# Revit family: HVAC_Mechanical-Ventilation_Ice-Air_HWCAC_Horizontal
name_source: partatom
category: Mechanical Equipment
revit_build: Autodesk Revit 2015 (Build: 20140606_1530(x64)
units: mm (PartAtom-declared; Revit-internal decimal feet)

## types (11) — shared parameters
2-pipe Inlet Description = Water Inlet Connection
2-pipe Outlet Description = Water Outlet Connection
Air Filter Material = Plastic - Ice_Air - Blue
BIMobject category = Air Conditioning
BIMobject category code = hvac-air-con
BIMobject main category = HVAC
BIMobject main category code = hvac
Brand url = http://www.ice-air.com
Condensate Connection = 0.75 "
Condensate Drain Description = Condensate Drain Connection
Date of publishing = 1/30/2014
Default Elevation = 48 "
Description = Conserve floor space with ICE AIRs Horizontal WSHPs - flexible control options, variable air discharge outlets, and easy service access provide superior design and installation options.
Design country = United States
Discharge Position = 12 "
Duct Description = Supply Air
Edition number = 1
Frequency = 60 Hz
IFC Classification = Heat Exchanger
Manufacturer = Ice Air
Manufacturer country = United States
Manufacturer name = Ice Air
Masterformat 2014 Code = 23 00 00
Masterformat 2014 Description = Heating, Ventilating, and Air Conditioning (HVAC)
NBS Reference Code = 03-03
NBS Reference Description = Air Conditioning Units
OmniClass Code = 23-33 39 11
OmniClass Description = Air Conditioners
Phase = 1
Product Guid = 5dc7aca0-5e98-4522-918c-9e6a5670b57e
Product SKU = horizontal_wshp_hybrid
Product data url = https://bimobject.com
Product family = Hybrid WCAC
Product group = Horizontal
Product url = http://www.ice-air.com
QR code = http://bimobject.com
Return Lenght = 25.4 "
Return Offset = 1.54 "
Steel Material = Steel - Ice_Air - Galvanized
Technical description = http://www.ice-air.com
UNSPSC Code = 40101701
URL = http://www.ice-air.com
Uniclass 1.4 Code = JU
Uniclass 1.4 Description = Ventilation and air conditioning systems
Uniclass 2.0 Code = PR-03-03
Uniclass 2.0 Description = Air Conditioning Units
Uniclass 2015 Code = EF_65_80
Uniclass 2015 Name = Air conditioning
Uniformat II Code = D3090
Uniformat II Description = Other HVAC Systems & Equipment
Voltage = 230 V
Voltage (Range) = 208 - 230 V
Weight Net (Kg) = 0
zero-valued in all types: Nominal height, Nominal width

## per-type parameters (varying)
| type | Air Flow | Discharge Height | Discharge Width | Energy Efficiency Rating w/ECM | Energy Efficiency Rating w/PSC | Flow Rate | Height | Inlet/Outlet Connection | Length | Total Cooling Capacity | Total Heating Capacity @ 105F EWT | Total Heating Capacity @ 120F EWT | Total Heating Capacity @ 95F EWT | Weight | Width | z Type |
| 8HHW09 | 300.0 CFM | 5 " | 10 " | 14.5 | 14 | 2.3 GPM | 12 " | 0.5 " | 34 " | 9300 Btu/h | 8500 Btu/h | 10500 Btu/h | 6300 Btu/h | 130 lbm | 20 " | 1 |
| 8HHW12 | 400.0 CFM | 5 " | 10 " | 14.1 | 13.5 | 3.0 GPM | 12 " | 0.5 " | 34 " | 12200 Btu/h | 12300 Btu/h | 16900 Btu/h | 9200 Btu/h | 140 lbm | 20 " | 2 |
| 8HHW15 | 500.0 CFM | 8 " | 9 " | 14.9 | 14.3 | 3.8 GPM | 17 " | 0.5 " | 42 " | 14900 Btu/h | 15500 Btu/h | 21000 Btu/h | 12000 Btu/h | 180 lbm | 20 " | 3 |
| 8HHW18 | 600.0 CFM | 8 " | 9 " | 14.6 | 14 | 4.5 GPM | 17 " | 0.75 " | 42 " | 19500 Btu/h | 18600 Btu/h | 25500 Btu/h | 15800 Btu/h | 220 lbm | 20 " | 4 |
| 8HHW24 | 800.0 CFM | 10 " | 11 " | 14.9 | 14.4 | 6.0 GPM | 18.25 " | 0.75 " | 42 " | 23500 Btu/h | 19800 Btu/h | 28000 Btu/h | 16700 Btu/h | 280 lbm | 20 " | 5 |
| 8HHW30 | 1000.0 CFM | 10 " | 11 " | 15.1 | 14.5 | 7.5 GPM | 18.25 " | 0.75 " | 42 " | 29100 Btu/h | 21900 Btu/h | 31200 Btu/h | 17800 Btu/h | 300 lbm | 20 " | 6 |
| 8HHW36 | 1200.0 CFM | 11 " | 12 " | 15.6 | 15 | 9.0 GPM | 20 " | 0.75 " | 46 " | 35000 Btu/h | 26300 Btu/h | 37400 Btu/h | 21300 Btu/h | 310 lbm | 21 " | 7 |
| 8HHW42 | 1400.0 CFM | 11 " | 12 " | 14.9 | 14.2 | 10.5 GPM | 20 " | 0.75 " | 46 " | 41500 Btu/h | 30600 Btu/h | 43700 Btu/h | 24900 Btu/h | 320 lbm | 21 " | 8 |
| 8HHW48 | 1600.0 CFM | 12 " | 13 " | 14.5 | 13.8 | 12.0 GPM | 23 " | 0.75 " | 52 " | 48300 Btu/h | 35100 Btu/h | 49900 Btu/h | 28500 Btu/h | 330 lbm | 28 " | 9 |
| 8HHW60 | 2000.0 CFM | 12 " | 13 " | 14.9 | 14.2 | 15.0 GPM | 23 " | 0.75 " | 52 " | 60000 Btu/h | 43800 Btu/h | 62400 Btu/h | 35600 Btu/h | 350 lbm | 28 " | 10 |
| 8HHW70 | 2400.0 CFM | 12 " | 13 " | 14.7 | 14 | 17.5 GPM | 23 " | 0.75 " | 52 " | 67000 Btu/h | 51500 Btu/h | 72800 Btu/h | 41500 Btu/h | 380 lbm | 28 " | 11 |

note: column(s) folded — value = type name in every type: Model

## geometry (parser evidence)
native form markers: Sweep x15
no freeform markers — native parametric forms only
